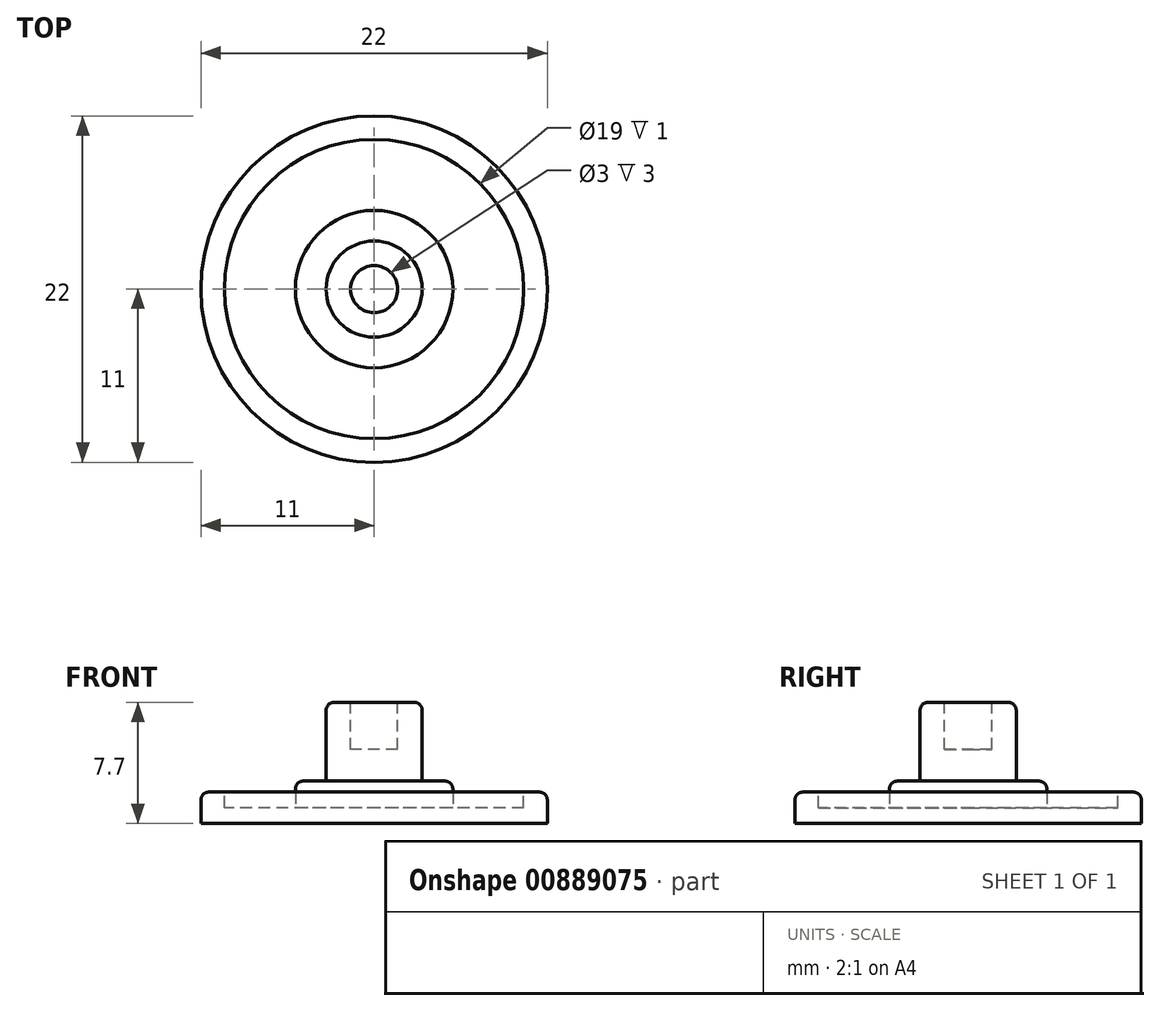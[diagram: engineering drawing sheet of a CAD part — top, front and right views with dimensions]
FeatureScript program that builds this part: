
annotation { "Feature Type Name" : "Feature", "Feature Type Description" : "" }
export const myFeature = defineFeature(function(context is Context, id is Id, definition is map)
    precondition{}
    {
        {
            var Q0;
            Q0=qCreatedBy(makeId("Top.planeOp"),FACE);
            var sketch = newSketch(context, id + "F0", { "sketchPlane" : qUnion([Q0])});
            skCircle(sketch, "E0", {"center": v(0, 0) * mm, "radius": 11 * mm});
            skSolve(sketch);
        }
        {
            var Q0;
            Q0=makeQuery(id+"F0.imprint","IMPRINT",FACE,{"disambiguationData":[TD([[makeQuery(id+"F0.imprint","IMPRINT",EDGE,{"derivedFrom":sQuery(id+"F0.wireOp",EDGE,"E0")}),1.0]])]});
            extrude(context, id + "F1", {"entities" : qUnion([Q0]), "depth" : 2 * mm, "offsetDistance" : 25 * mm});
        }
        {
            var Q0;
            Q0=makeQuery(id+"F1.opExtrude","CAP_FACE",FACE,{"disambiguationData":[OSD([sQuery(id+"F0.wireOp",EDGE,"E0")])],"isStart":false});
            var sketch = newSketch(context, id + "F2", { "sketchPlane" : qUnion([Q0])});
            skCircle(sketch, "E1", {"center": v(0, 0) * mm, "radius": 9.5 * mm});
            skSolve(sketch);
        }
        {
            var Q0;
            Q0 = qSketchRegion(id + "F2", true);
            extrude(context, id + "F3", {"entities" : qUnion([Q0]), "operationType" : NewBodyOperationType.REMOVE, "oppositeDirection" : true, "depth" : 1 * mm, "offsetDistance" : 25 * mm});
        }
        {
            var Q0;
            Q0=makeQuery(id+"F3.boolean.opBoolean","COPY",FACE,{"derivedFrom":makeQuery(id+"F3.opExtrude","CAP_FACE",FACE,{"disambiguationData":[OSD([sQuery(id+"F2.wireOp",EDGE,"E1")])],"isStart":false})});
            var sketch = newSketch(context, id + "F4", { "sketchPlane" : qUnion([Q0])});
            skCircle(sketch, "E2", {"center": v(0, 0) * mm, "radius": 5 * mm});
            skSolve(sketch);
        }
        {
            var Q0;
            Q0=makeQuery(id+"F4.imprint","IMPRINT",FACE,{"disambiguationData":[TD([[makeQuery(id+"F4.imprint","IMPRINT",EDGE,{"derivedFrom":sQuery(id+"F4.wireOp",EDGE,"E2")}),1.0]])]});
            extrude(context, id + "F5", {"entities" : qUnion([Q0]), "operationType" : NewBodyOperationType.ADD, "depth" : 1.7 * mm, "offsetDistance" : 25 * mm});
        }
        {
            var Q0;
            Q0=makeQuery(id+"F5.opExtrude","CAP_FACE",FACE,{"disambiguationData":[OSD([sQuery(id+"F4.wireOp",EDGE,"E2")])],"isStart":false});
            var sketch = newSketch(context, id + "F6", { "sketchPlane" : qUnion([Q0])});
            skCircle(sketch, "E3", {"center": v(0, 0) * mm, "radius": 3.05 * mm});
            skSolve(sketch);
        }
        {
            var Q0;
            Q0=makeQuery(id+"F6.imprint","IMPRINT",FACE,{"disambiguationData":[TD([[makeQuery(id+"F6.imprint","IMPRINT",EDGE,{"derivedFrom":sQuery(id+"F6.wireOp",EDGE,"E3")}),1.0]])]});
            extrude(context, id + "F7", {"entities" : qUnion([Q0]), "operationType" : NewBodyOperationType.ADD, "depth" : 5 * mm, "offsetDistance" : 25 * mm});
        }
        {
            var Q0;
            Q0=makeQuery(id+"F7.opExtrude","CAP_FACE",FACE,{"disambiguationData":[OSD([sQuery(id+"F6.wireOp",EDGE,"E3")])],"isStart":false});
            var sketch = newSketch(context, id + "F8", { "sketchPlane" : qUnion([Q0])});
            skCircle(sketch, "E4", {"center": v(0, 0) * mm, "radius": 1.5 * mm});
            skSolve(sketch);
        }
        {
            var Q0;
            Q0=makeQuery(id+"F8.imprint","IMPRINT",FACE,{"disambiguationData":[TD([[makeQuery(id+"F8.imprint","IMPRINT",EDGE,{"derivedFrom":sQuery(id+"F8.wireOp",EDGE,"E4")}),1.0]])]});
            extrude(context, id + "F9", {"entities" : qUnion([Q0]), "operationType" : NewBodyOperationType.REMOVE, "oppositeDirection" : true, "depth" : 3 * mm, "offsetDistance" : 25 * mm});
        }
        {
            var Q0;
            Q0=makeQuery(id+"F3.boolean.opBoolean","COPY",EDGE,{"derivedFrom":makeQuery(id+"F3.opExtrude","CAP_EDGE",EDGE,{"disambiguationData":[OSD([sQuery(id+"F2.wireOp",EDGE,"E1")])],"isStart":true})});
            var Q1;
            Q1=makeQuery(id+"F1.opExtrude","CAP_EDGE",EDGE,{"disambiguationData":[OSD([sQuery(id+"F0.wireOp",EDGE,"E0")])],"isStart":false});
            var Q2;
            Q2=makeQuery(id+"F7.opExtrude","CAP_EDGE",EDGE,{"disambiguationData":[OSD([sQuery(id+"F6.wireOp",EDGE,"E3")])],"isStart":false});
            var Q3;
            Q3=makeQuery(id+"F5.opExtrude","CAP_EDGE",EDGE,{"disambiguationData":[OSD([sQuery(id+"F4.wireOp",EDGE,"E2")])],"isStart":false});
            fillet(context, id + "F10", {"entities" : qUnion([Q0, Q1, Q2, Q3]), "radius" : .5 * mm, "tangentPropagation" : true, "allowEdgeOverflow" : false});
        }
    });
